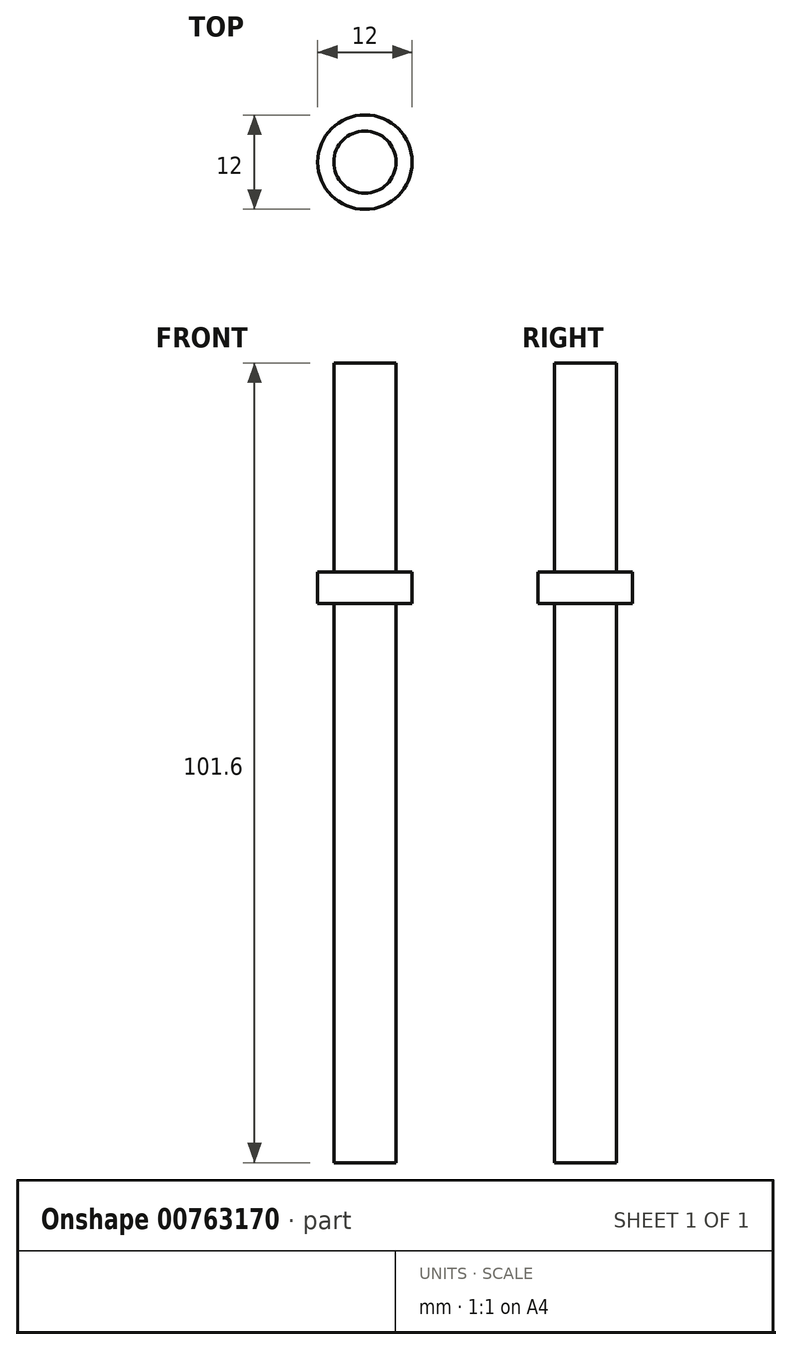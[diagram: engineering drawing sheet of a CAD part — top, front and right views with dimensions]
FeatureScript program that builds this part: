
annotation { "Feature Type Name" : "Feature", "Feature Type Description" : "" }
export const myFeature = defineFeature(function(context is Context, id is Id, definition is map)
    precondition{}
    {
        {
            var Q0;
            Q0=qCreatedBy(makeId("Top.planeOp"),FACE);
            var sketch = newSketch(context, id + "F0", { "sketchPlane" : qUnion([Q0])});
            skCircle(sketch, "E0", {"center": v(0, 0) * mm, "radius": 3.95 * mm});
            skSolve(sketch);
        }
        {
            var Q0;
            Q0 = qSketchRegion(id + "F0", true);
            extrude(context, id + "F1", {"entities" : qUnion([Q0]), "depth" : 101.6 * mm, "offsetDistance" : 25 * mm});
        }
        {
            var Q0;
            Q0=qCreatedBy(makeId("Top.planeOp"),FACE);
            cPlane(context, id + "F2", {"entities" : qUnion([Q0]), "cplaneType" : CPlaneType.OFFSET, "offset" : 75 * mm, "width" : 150 * mm, "height" : 150 * mm});
        }
        {
            var Q0;
            Q0=qCreatedBy(id+"F2.planeOp",FACE);
            var sketch = newSketch(context, id + "F3", { "sketchPlane" : qUnion([Q0])});
            skCircle(sketch, "E1", {"center": v(0, 0) * mm, "radius": 6 * mm});
            skSolve(sketch);
        }
        {
            var Q0;
            Q0=makeQuery(id+"F3.imprint","IMPRINT",FACE,{"disambiguationData":[TD([[makeQuery(id+"F3.imprint","IMPRINT",EDGE,{"derivedFrom":sQuery(id+"F3.wireOp",EDGE,"E1")}),1.0]])]});
            extrude(context, id + "F4", {"entities" : qUnion([Q0]), "operationType" : NewBodyOperationType.ADD, "oppositeDirection" : true, "depth" : 4 * mm, "offsetDistance" : 25 * mm});
        }
    });
